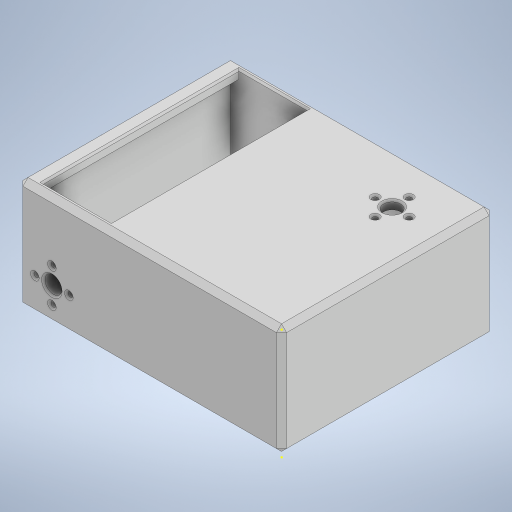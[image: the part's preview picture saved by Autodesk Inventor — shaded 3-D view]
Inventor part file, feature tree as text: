
AUTODESK INVENTOR PART (.ipt)
format: ipt  version: 2023 (Build 270158000, 158)  size: 328,192 bytes
history: native  units: mm
features: sketch x16, extrude x10, chamfer x4
ambient origin geometry x8: Origin, YZ Plane, XZ Plane, XY Plane, X Axis, Y Axis, Z Axis, Center Point
bodies: Solid1 (feature_tree)
feature tree (30):
  extrude  "Extrusion1"  Depth=155.0mm
  extrude  "Extrusion2"  Depth=5.0mm
  extrude  "Extrusion3"  Depth=5.0mm
  extrude  "Extrusion4"  Depth=55.0mm TaperAngle=0.0deg
  extrude  "Extrusion5"  Depth=10.0mm
  extrude  "Extrusion6"  Depth=30.0mm
  extrude  "Extrusion7"  Depth=5.0mm
  sketch  "Sketch8"  dims[d18=20.0mm d19=10.0mm d20=20.0mm d21=0.0mm]
  sketch  "Sketch9"  dims[d22=10.0mm]
  sketch  "Sketch10"  dims[d23=5.0mm]
  extrude  "Extrusion8"  Depth=10.0mm
  chamfer  "Chamfer1"  Distance=20.0mm
  chamfer  "Chamfer3"  Distance=5.0mm
  extrude  "Extrusion9"  Depth=40.0mm TaperAngle=360.0deg
  sketch  "Sketch13"  dims[d28=3.0mm d29=40.0mm d31=360.0deg]
  extrude  "Extrusion10"  Depth=10.0mm
  chamfer  "Chamfer4"  Distance=40.0mm Angle=360.0deg
  chamfer  "Chamfer5"  Distance=5.0mm
  sketch  "Sketch15"  dims[d36=10.0mm]
  sketch  "Sketch16"  dims[d37=3.0mm d38=40.0mm d40=360.0deg d42=5.0mm d43=0.0mm d44=1.0mm d45=2.0mm d46=45.0deg d50=1.0mm d51=2.0mm d52=45.0deg d53=30.0mm d54=30.0mm d55=5.0mm d56=0.0mm d57=20.0mm d58=0.0mm d59=1.0mm d60=2.0mm d61=45.0deg d62=3.0mm d63=2.0mm d64=45.0deg d30=0.872665mm d32=0.872665mm]
  sketch  "Sketch1"  dims[d0=125.0mm d1=155.0mm]
  sketch  "Sketch2"  dims[d2=60.0mm d3=0.0mm d4=5.0mm]
  sketch  "Sketch3"  dims[d5=5.0mm d6=5.0mm]
  sketch  "Sketch4"  dims[d7=5.0mm d8=55.0mm d9=0.0mm]
  sketch  "Sketch5"  dims[d10=5.0mm d11=0.0mm d12=10.0mm]
  sketch  "Sketch6"  dims[d13=30.0mm d14=30.0mm]
  sketch  "Sketch7"  dims[d15=5.0mm d16=0.0mm d17=20.0mm]
  sketch  "Sketch11"  dims[d24=5.0mm]
  sketch  "Sketch12"  dims[d25=40.0mm d26=5.0mm d27=0.0mm]
  sketch  "Sketch14"  dims[d33=5.0mm d34=0.0mm d35=10.0mm]
